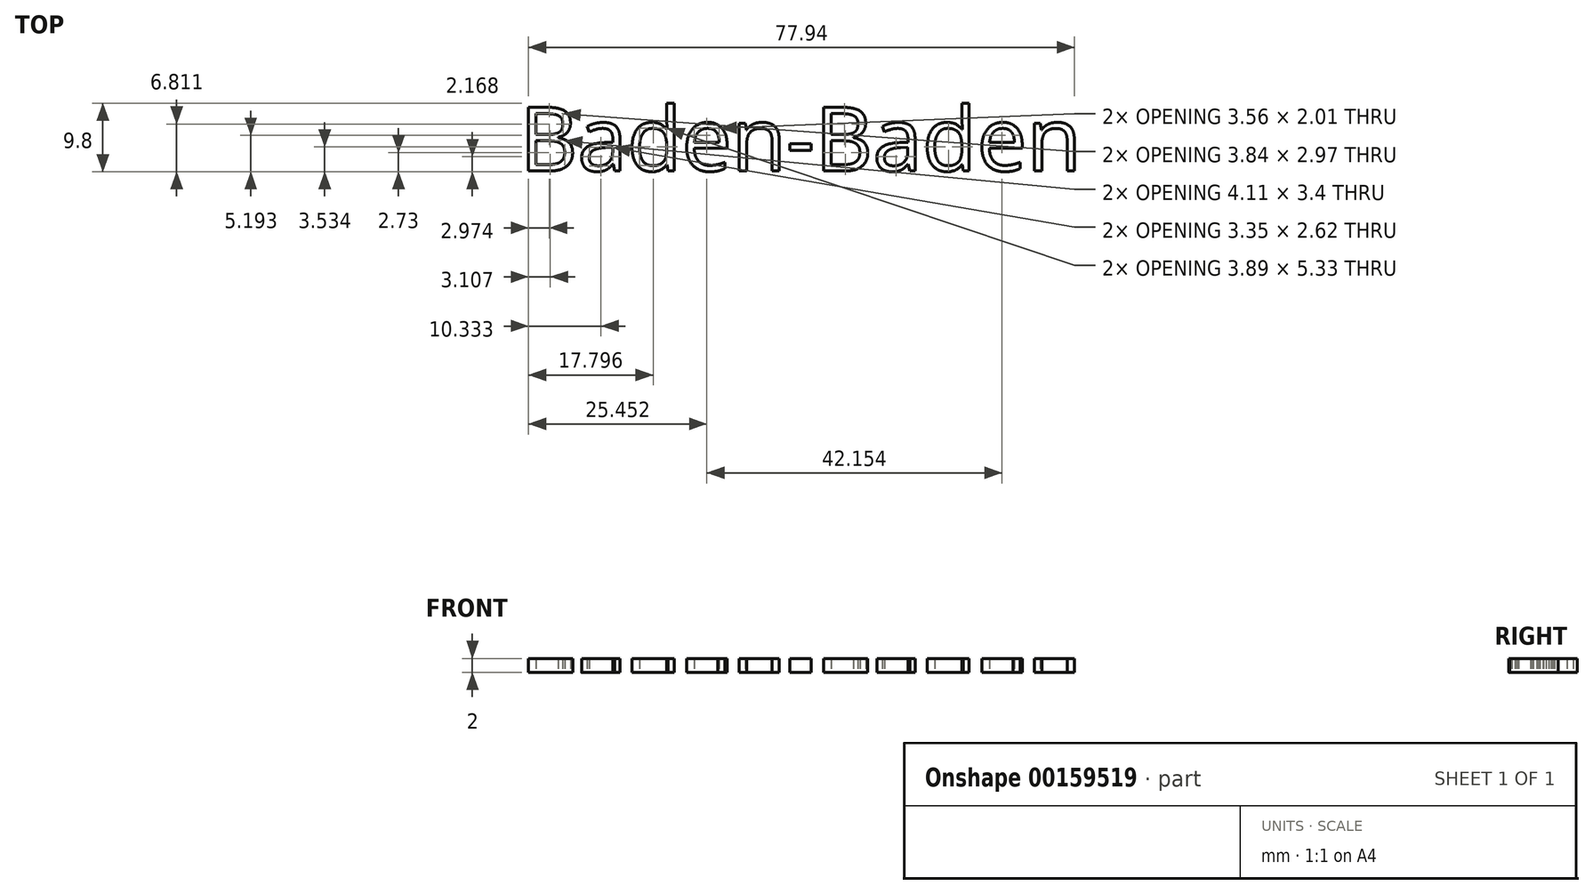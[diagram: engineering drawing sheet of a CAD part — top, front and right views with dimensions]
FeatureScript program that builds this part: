
annotation { "Feature Type Name" : "Feature", "Feature Type Description" : "" }
export const myFeature = defineFeature(function(context is Context, id is Id, definition is map)
    precondition{}
    {
        {
            var Q0;
            Q0=qCreatedBy(makeId("Top.planeOp"),FACE);
            var sketch = newSketch(context, id + "F0", { "sketchPlane" : qUnion([Q0])});
            skText(sketch, "E0", { "text": "Baden-Baden", "fontName": "OpenSans-Regular.ttf"});
            const initialGuessF0  = {"E0": [-0.0157, -0.00772, 1, 0, 0.00916]};
            skSetInitialGuess(sketch, initialGuessF0);
            skSolve(sketch);
        }
        {
            var Q0;
            Q0 = qSketchRegion(id + "F0", true);
            extrude(context, id + "F1", {"entities" : qUnion([Q0]), "depth" : 2 * mm});
        }
    });
